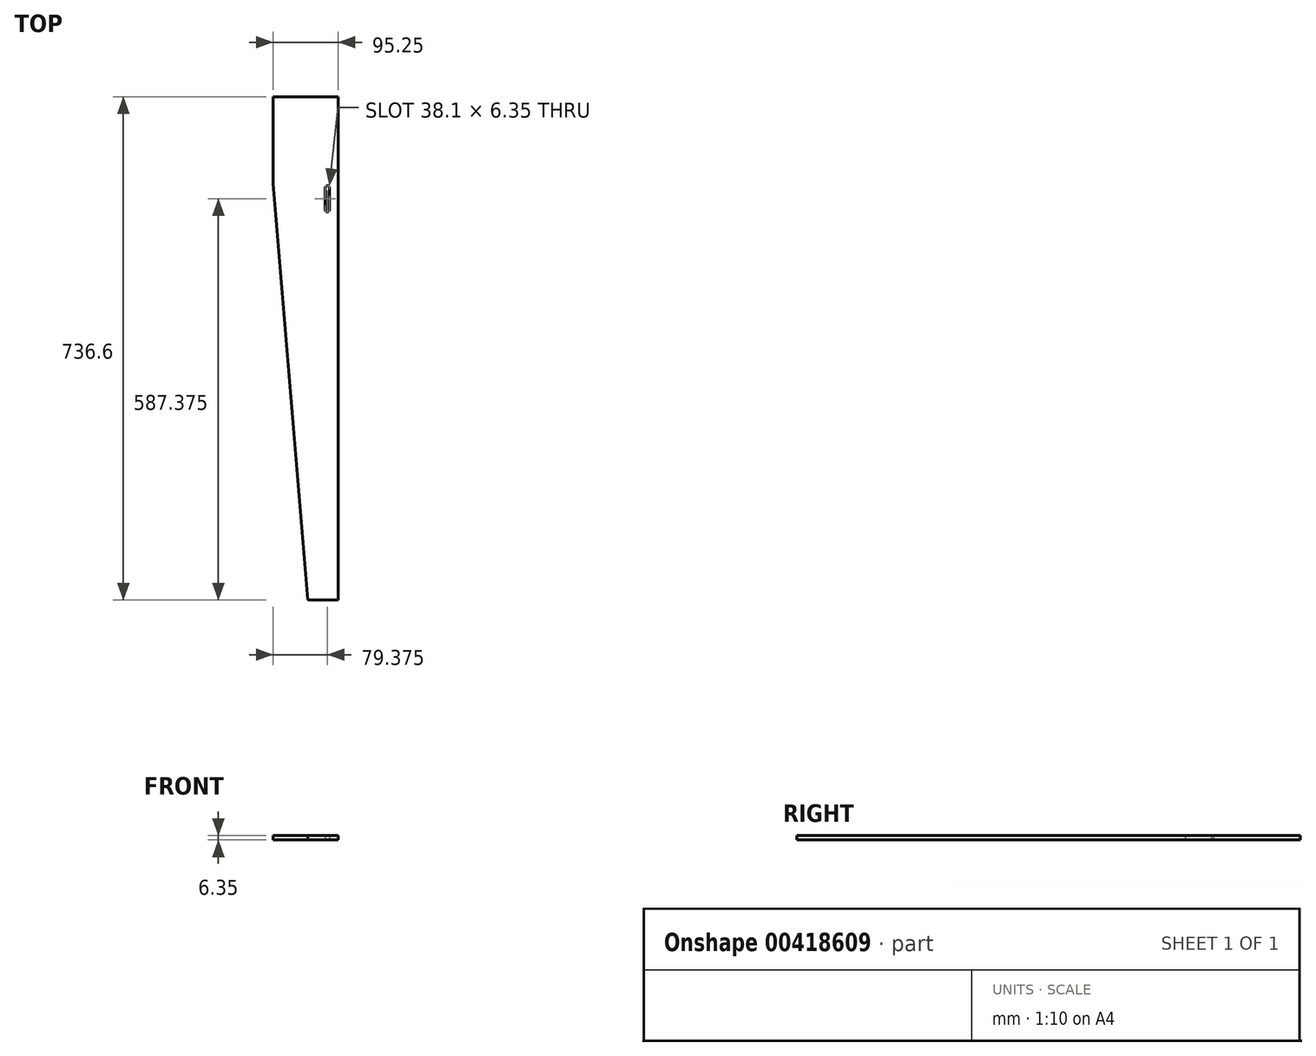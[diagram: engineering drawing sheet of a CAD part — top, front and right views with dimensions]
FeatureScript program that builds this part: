
annotation { "Feature Type Name" : "Feature", "Feature Type Description" : "" }
export const myFeature = defineFeature(function(context is Context, id is Id, definition is map)
    precondition{}
    {
        {
            var Q0;
            Q0=qCreatedBy(makeId("Top.planeOp"),FACE);
            var sketch = newSketch(context, id + "F0", { "sketchPlane" : qUnion([Q0])});
            skLineSegment(sketch, "E0.bottom", {"start": v(6.35, 0) * mm, "end": v(101.6, 0) * mm});
            skLineSegment(sketch, "E0.top", {"start": v(6.35, -736.6) * mm, "end": v(50.8, -736.6) * mm});
            skLineSegment(sketch, "E0.right", {"start": v(101.6, 0) * mm, "end": v(101.6, -127) * mm});
            skLineSegment(sketch, "E1", {"start": v(101.6, -127) * mm, "end": v(50.8, -736.6) * mm});
            skLineSegment(sketch, "E2.left", {"start": v(25.4, -133.35) * mm, "end": v(25.4, -165.1) * mm});
            skLineSegment(sketch, "E2.right", {"start": v(19.05, -133.35) * mm, "end": v(19.05, -165.1) * mm});
            skArc(sketch, "E3", {"start": v(19.05, -165.1) * mm, "mid": v(22.23, -168.28) * mm, "end": v(25.4, -165.1) * mm});
            skLineSegment(sketch, "E4.0", {"start": v(6.35, 0) * mm, "end": v(6.35, -736.6) * mm});
            skArc(sketch, "E5", {"start": v(25.4, -133.35) * mm, "mid": v(22.23, -130.17) * mm, "end": v(19.05, -133.35) * mm});
            skPoint(sketch, "E6.orphan", {"position": v(22.23, -127) * mm});
            skPoint(sketch, "E7.orphan", {"position": v(25.4, -127) * mm});
            skPoint(sketch, "E8.orphan", {"position": v(19.05, -127) * mm});
            skSolve(sketch);
        }
        {
            var Q0;
            Q0=qSketchRegion(id+"F0",true);
            extrude(context, id + "F1", {"entities" : qUnion([Q0]), "depth" : 6.35 * mm});
        }
        {
            var Q0;
            Q0=makeQuery(id+"F1.opExtrude","SWEPT_BODY",BODY,{"disambiguationData":[OSD([sQuery(id+"F0.wireOp",EDGE,"E0.bottom"),sQuery(id+"F0.wireOp",EDGE,"E0.left"),sQuery(id+"F0.wireOp",EDGE,"E0.top"),sQuery(id+"F0.wireOp",EDGE,"E0.right"),sQuery(id+"F0.wireOp",EDGE,"E1"),sQuery(id+"F0.wireOp",EDGE,"E2.left"),sQuery(id+"F0.wireOp",EDGE,"E2.right"),sQuery(id+"F0.wireOp",EDGE,"KLRdM56R-qGYC-7aCV-vhcM-UEOSVXzbKlv8"),sQuery(id+"F0.wireOp",EDGE,"E3")])]});
            var Q1;
            Q1=qCreatedBy(makeId("Right.planeOp"),FACE);
            mirror(context, id + "F2", {"entities" : qUnion([Q0]), "mirrorPlane" : qUnion([Q1])});
        }
        {
            var Q0;
            Q0=makeQuery(id+"F1.opExtrude","SWEPT_BODY",BODY,{"disambiguationData":[OSD([sQuery(id+"F0.wireOp",EDGE,"E0.bottom"),sQuery(id+"F0.wireOp",EDGE,"E0.left"),sQuery(id+"F0.wireOp",EDGE,"E0.top"),sQuery(id+"F0.wireOp",EDGE,"E0.right"),sQuery(id+"F0.wireOp",EDGE,"E1"),sQuery(id+"F0.wireOp",EDGE,"E2.left"),sQuery(id+"F0.wireOp",EDGE,"E2.right"),sQuery(id+"F0.wireOp",EDGE,"KLRdM56R-qGYC-7aCV-vhcM-UEOSVXzbKlv8"),sQuery(id+"F0.wireOp",EDGE,"E3")])]});
            deleteBodies(context, id + "F3", {"entities" : qUnion([Q0])});
        }
    });
